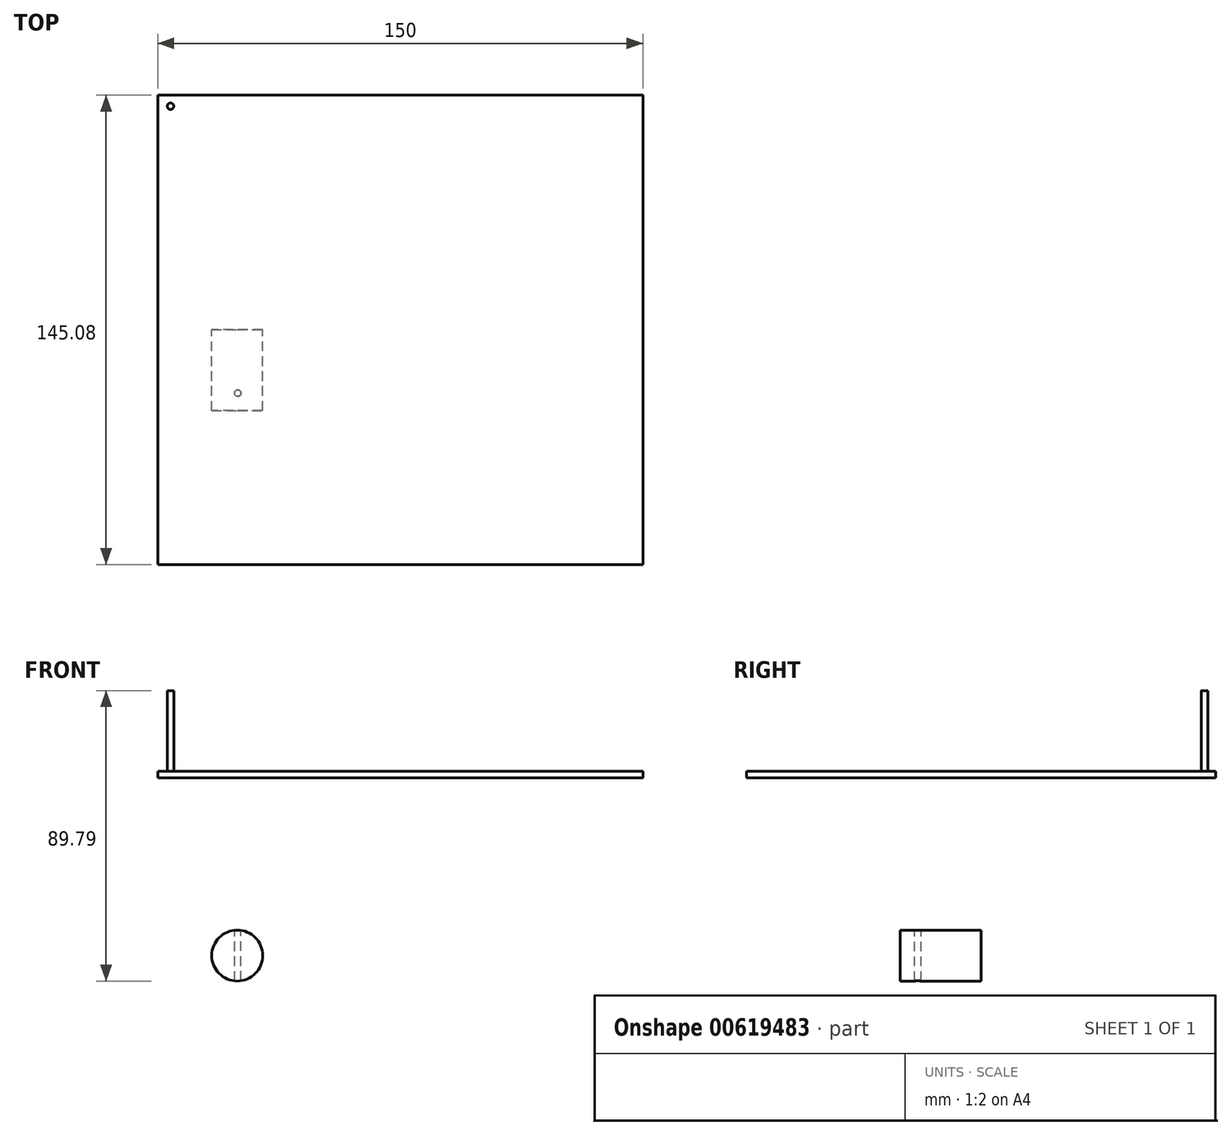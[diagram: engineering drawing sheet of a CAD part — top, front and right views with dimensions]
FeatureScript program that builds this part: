
annotation { "Feature Type Name" : "Feature", "Feature Type Description" : "" }
export const myFeature = defineFeature(function(context is Context, id is Id, definition is map)
    precondition{}
    {
        {
            var Q0;
            Q0=qCreatedBy(makeId("Top.planeOp"),FACE);
            var sketch = newSketch(context, id + "F0", { "sketchPlane" : qUnion([Q0])});
            skLineSegment(sketch, "E0.bottom", {"start": v(-75, 72.54) * mm, "end": v(75, 72.54) * mm});
            skLineSegment(sketch, "E0.top", {"start": v(-75, -72.54) * mm, "end": v(75, -72.54) * mm});
            skLineSegment(sketch, "E0.left", {"start": v(-75, 72.54) * mm, "end": v(-75, -72.54) * mm});
            skLineSegment(sketch, "E0.right", {"start": v(75, 72.54) * mm, "end": v(75, -72.54) * mm});
            skPoint(sketch, "E0.middle", {"position": v(0, 0) * mm});
            skSolve(sketch);
        }
        {
            var Q0;
            Q0 = qSketchRegion(id + "F0", true);
            extrude(context, id + "F1", {"entities" : qUnion([Q0]), "depth" : 2 * mm, "offsetDistance" : 25 * mm});
        }
        {
            var Q0;
            Q0=makeQuery(id+"F1.opExtrude","CAP_FACE",FACE,{"disambiguationData":[OSD([sQuery(id+"F0.wireOp",EDGE,"E0.bottom"),sQuery(id+"F0.wireOp",EDGE,"E0.top"),sQuery(id+"F0.wireOp",EDGE,"E0.left"),sQuery(id+"F0.wireOp",EDGE,"E0.right")])],"isStart":false});
            var sketch = newSketch(context, id + "F2", { "sketchPlane" : qUnion([Q0])});
            skCircle(sketch, "E1", {"center": v(-71.07, 69.12) * mm, "radius": 1 * mm});
            skSolve(sketch);
        }
        {
            var Q0;
            Q0 = qSketchRegion(id + "F2", true);
            extrude(context, id + "F3", {"entities" : qUnion([Q0]), "depth" : 25 * mm, "offsetDistance" : 25 * mm});
        }
        {
            var Q0;
            Q0=qCreatedBy(makeId("Front.planeOp"),FACE);
            var sketch = newSketch(context, id + "F4", { "sketchPlane" : qUnion([Q0])});
            skCircle(sketch, "E2", {"center": v(-50.44, -54.92) * mm, "radius": 7.87 * mm});
            skSolve(sketch);
        }
        {
            var Q0;
            Q0=makeQuery(id+"F4.imprint","IMPRINT",FACE,{"disambiguationData":[TD([[makeQuery(id+"F4.imprint","IMPRINT",EDGE,{"derivedFrom":sQuery(id+"F4.wireOp",EDGE,"E2")}),1.0]])]});
            extrude(context, id + "F5", {"entities" : qUnion([Q0]), "depth" : 25 * mm, "offsetDistance" : 25 * mm});
        }
        {
            var Q0;
            Q0=makeQuery(id+"F1.opExtrude","CAP_FACE",FACE,{"disambiguationData":[OSD([sQuery(id+"F0.wireOp",EDGE,"E0.bottom"),sQuery(id+"F0.wireOp",EDGE,"E0.top"),sQuery(id+"F0.wireOp",EDGE,"E0.left"),sQuery(id+"F0.wireOp",EDGE,"E0.right")])],"isStart":true});
            var sketch = newSketch(context, id + "F6", { "sketchPlane" : qUnion([Q0])});
            skPoint(sketch, "E3", {"position": v(-50.26, 19.59) * mm});
            skSolve(sketch);
        }
        {
            var Q0;
            Q0=sQuery(id+"F6.wireOp",VERTEX,"E3");
            var Q1;
            Q1=makeQuery(id+"F5.opExtrude","SWEPT_BODY",BODY,{"disambiguationData":[OSD([sQuery(id+"F4.wireOp",EDGE,"E2")])]});
            hole(context, id + "F7", {"style" : HoleStyle.SIMPLE, "endStyle" : HoleEndStyle.BLIND, "oppositeDirection" : true, "holeDiameter" : 2 * mm, "majorDiameter" : 5 * mm, "holeDepth" : 150 * mm, "isTappedThrough" : true, "tappedDepth" : 12 * mm, "tapClearance" : 3, "locations" : qUnion([Q0]), "scope" : qUnion([Q1])});
        }
    });
